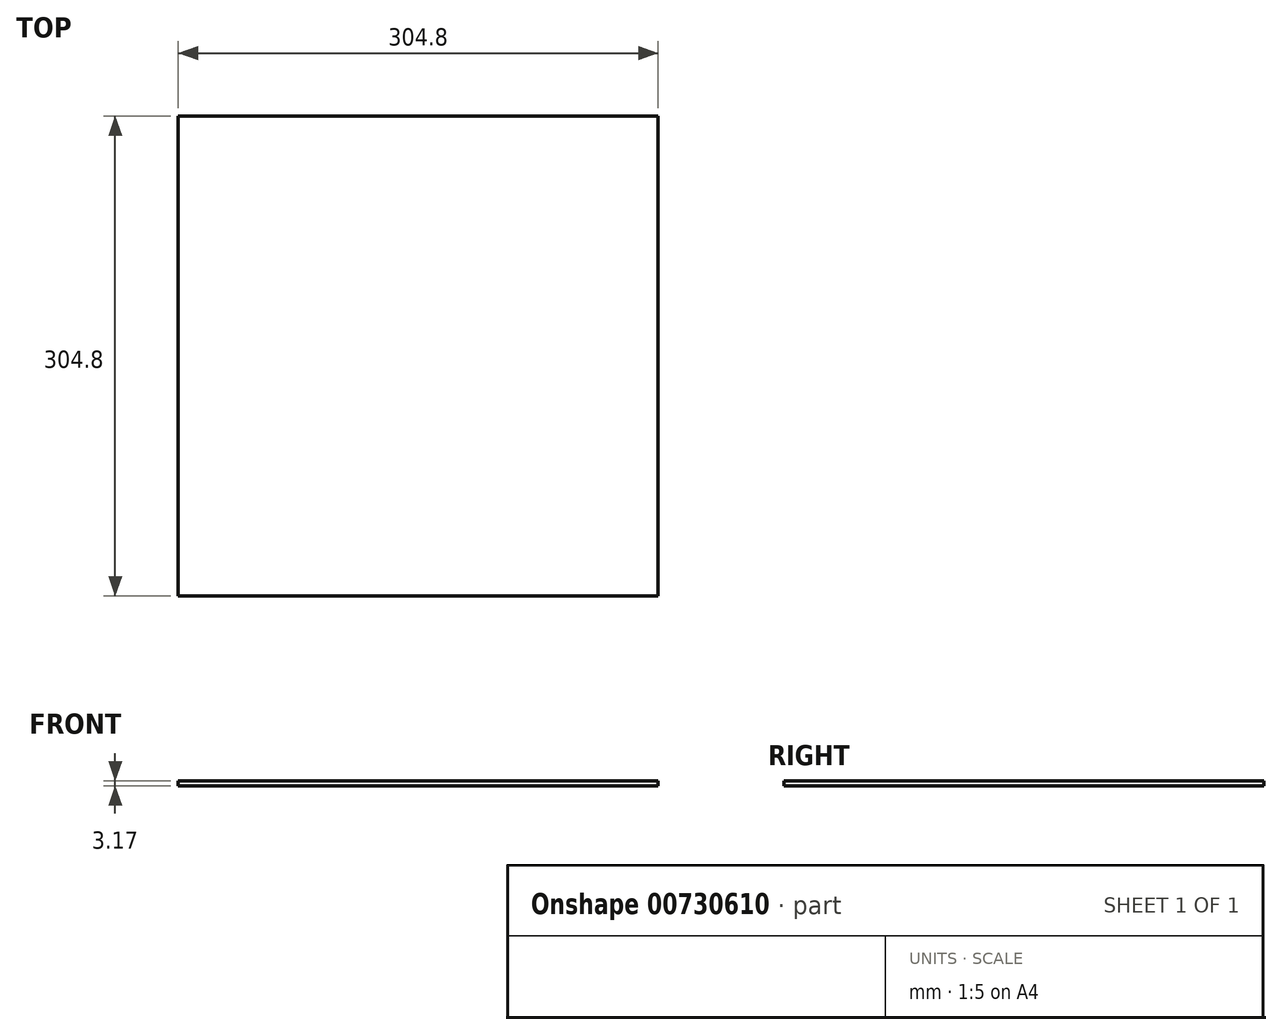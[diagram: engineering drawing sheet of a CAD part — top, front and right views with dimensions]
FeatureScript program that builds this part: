
annotation { "Feature Type Name" : "Feature", "Feature Type Description" : "" }
export const myFeature = defineFeature(function(context is Context, id is Id, definition is map)
    precondition{}
    {
        {
            var Q0;
            Q0=qCreatedBy(makeId("Top.planeOp"),FACE);
            var sketch = newSketch(context, id + "F0", { "sketchPlane" : qUnion([Q0])});
            skLineSegment(sketch, "E0.bottom", {"start": v(-152.4, 152.4) * mm, "end": v(152.4, 152.4) * mm});
            skLineSegment(sketch, "E0.top", {"start": v(-152.4, -152.4) * mm, "end": v(152.4, -152.4) * mm});
            skLineSegment(sketch, "E0.left", {"start": v(-152.4, 152.4) * mm, "end": v(-152.4, -152.4) * mm});
            skLineSegment(sketch, "E0.right", {"start": v(152.4, 152.4) * mm, "end": v(152.4, -152.4) * mm});
            skPoint(sketch, "E0.middle", {"position": v(0, 0) * mm});
            skSolve(sketch);
        }
        {
            var Q0;
            Q0=makeQuery(id+"F0.imprint","IMPRINT",FACE,{"disambiguationData":[TD([[makeQuery(id+"F0.imprint","IMPRINT",EDGE,{"derivedFrom":sQuery(id+"F0.wireOp",EDGE,"E0.bottom")}),-1.0]])]});
            extrude(context, id + "F1", {"entities" : qUnion([Q0]), "depth" : 3.17 * mm, "offsetDistance" : 25.4 * mm});
        }
    });
